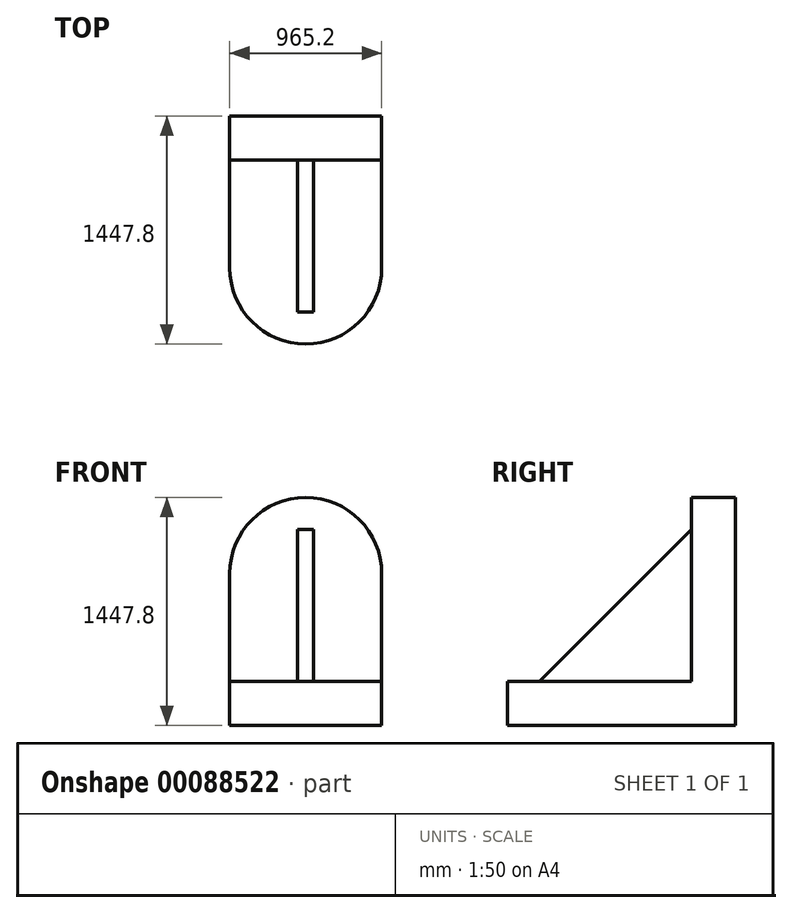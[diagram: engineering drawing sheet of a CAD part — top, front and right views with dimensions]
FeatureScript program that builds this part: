
annotation { "Feature Type Name" : "Feature", "Feature Type Description" : "" }
export const myFeature = defineFeature(function(context is Context, id is Id, definition is map)
    precondition{}
    {
        {
            var Q0;
            Q0=qCreatedBy(makeId("Top.planeOp"),FACE);
            var sketch = newSketch(context, id + "F0", { "sketchPlane" : qUnion([Q0])});
            skLineSegment(sketch, "E0.bottom", {"start": v(-482.6, 482.6) * mm, "end": v(482.6, 482.6) * mm});
            skLineSegment(sketch, "E0.top", {"start": v(-482.6, -482.6) * mm, "end": v(482.6, -482.6) * mm});
            skLineSegment(sketch, "E0.left", {"start": v(-482.6, 482.6) * mm, "end": v(-482.6, -482.6) * mm});
            skLineSegment(sketch, "E0.right", {"start": v(482.6, 482.6) * mm, "end": v(482.6, -482.6) * mm});
            skSolve(sketch);
        }
        {
            var Q0;
            Q0=makeQuery(id+"F0.imprint","IMPRINT",FACE,{"disambiguationData":[TD([[makeQuery(id+"F0.imprint","IMPRINT",EDGE,{"derivedFrom":sQuery(id+"F0.wireOp",EDGE,"E0.bottom")}),-1.0]])]});
            extrude(context, id + "F1", {"entities" : qUnion([Q0]), "endBound" : BoundingType.SYMMETRIC, "depth" : 965.2 * mm});
        }
        {
            var Q0;
            Q0=makeQuery(id+"F1.opExtrude","SWEPT_FACE",FACE,{"disambiguationData":[OSD([sQuery(id+"F0.wireOp",EDGE,"E0.left")])]});
            var sketch = newSketch(context, id + "F2", { "sketchPlane" : qUnion([Q0])});
            skLineSegment(sketch, "E1.bottom", {"start": v(-203.2, 482.6) * mm, "end": v(482.6, 482.6) * mm});
            skLineSegment(sketch, "E1.top", {"start": v(-203.2, -203.2) * mm, "end": v(482.6, -203.2) * mm});
            skLineSegment(sketch, "E1.left", {"start": v(-203.2, 482.6) * mm, "end": v(-203.2, -203.2) * mm});
            skLineSegment(sketch, "E1.right", {"start": v(482.6, 482.6) * mm, "end": v(482.6, -203.2) * mm});
            skSolve(sketch);
        }
        {
            var Q0;
            Q0=makeQuery(id+"F2.imprint","IMPRINT",FACE,{"disambiguationData":[TD([[makeQuery(id+"F2.imprint","IMPRINT",EDGE,{"derivedFrom":sQuery(id+"F2.wireOp",EDGE,"E1.bottom")}),-1.0]])]});
            extrude(context, id + "F3", {"entities" : qUnion([Q0]), "operationType" : NewBodyOperationType.REMOVE, "endBound" : BoundingType.THROUGH_ALL, "oppositeDirection" : true, "depth" : 25.4 * mm});
        }
        {
            var Q0;
            Q0=makeQuery(id+"F3.boolean.opBoolean","COPY",FACE,{"derivedFrom":makeQuery(id+"F3.opExtrude","SWEPT_FACE",FACE,{"disambiguationData":[OSD([sQuery(id+"F2.wireOp",EDGE,"E1.left")])]})});
            var sketch = newSketch(context, id + "F4", { "sketchPlane" : qUnion([Q0])});
            skArc(sketch, "E2", {"start": v(482.6, 482.6) * mm, "mid": v(0, 965.2) * mm, "end": v(-482.6, 482.6) * mm});
            skSolve(sketch);
        }
        {
            var Q0;
            Q0=makeQuery(id+"F4.imprint","IMPRINT",FACE,{"disambiguationData":[TD([[makeQuery(id+"F4.imprint","IMPRINT",EDGE,{"derivedFrom":sQuery(id+"F4.wireOp",EDGE,"E2")}),1.0]])]});
            var Q1;
            Q1=makeQuery(id+"F1.opExtrude","SWEPT_FACE",FACE,{"disambiguationData":[OSD([sQuery(id+"F0.wireOp",EDGE,"E0.bottom")])]});
            extrude(context, id + "F5", {"entities" : qUnion([Q0]), "operationType" : NewBodyOperationType.ADD, "endBound" : BoundingType.UP_TO_SURFACE, "oppositeDirection" : true, "endBoundEntityFace" : qUnion([Q1]), "depth" : 25.4 * mm});
        }
        {
            var Q0;
            Q0=makeQuery(id+"F3.boolean.opBoolean","COPY",FACE,{"derivedFrom":makeQuery(id+"F3.opExtrude","SWEPT_FACE",FACE,{"disambiguationData":[OSD([sQuery(id+"F2.wireOp",EDGE,"E1.top")])]})});
            var sketch = newSketch(context, id + "F6", { "sketchPlane" : qUnion([Q0])});
            skArc(sketch, "E3", {"start": v(-482.6, -482.6) * mm, "mid": v(0, -965.2) * mm, "end": v(482.6, -482.6) * mm});
            skSolve(sketch);
        }
        {
            var Q0;
            Q0=makeQuery(id+"F6.imprint","IMPRINT",FACE,{"disambiguationData":[TD([[makeQuery(id+"F6.imprint","IMPRINT",EDGE,{"derivedFrom":sQuery(id+"F6.wireOp",EDGE,"E3")}),1.0]])]});
            var Q1;
            Q1=makeQuery(id+"F1.opExtrude","CAP_FACE",FACE,{"disambiguationData":[OSD([sQuery(id+"F0.wireOp",EDGE,"E0.bottom"),sQuery(id+"F0.wireOp",EDGE,"E0.top"),sQuery(id+"F0.wireOp",EDGE,"E0.left"),sQuery(id+"F0.wireOp",EDGE,"E0.right")])],"isStart":true});
            extrude(context, id + "F7", {"entities" : qUnion([Q0]), "operationType" : NewBodyOperationType.ADD, "endBound" : BoundingType.UP_TO_SURFACE, "oppositeDirection" : true, "endBoundEntityFace" : qUnion([Q1]), "depth" : 25.4 * mm});
        }
        {
            var Q0;
            Q0=qCreatedBy(makeId("Right.planeOp"),FACE);
            var sketch = newSketch(context, id + "F8", { "sketchPlane" : qUnion([Q0])});
            skLineSegment(sketch, "E4", {"start": v(203.2, -203.2) * mm, "end": v(-762, -203.2) * mm});
            skLineSegment(sketch, "E5", {"start": v(-762, -203.2) * mm, "end": v(203.2, 762) * mm});
            skLineSegment(sketch, "E6", {"start": v(203.2, 762) * mm, "end": v(203.2, -203.2) * mm});
            skSolve(sketch);
        }
        {
            var Q0;
            Q0=makeQuery(id+"F8.imprint","IMPRINT",FACE,{"disambiguationData":[TD([[makeQuery(id+"F8.imprint","IMPRINT",EDGE,{"derivedFrom":sQuery(id+"F8.wireOp",EDGE,"E4")}),-1.0]])]});
            extrude(context, id + "F9", {"entities" : qUnion([Q0]), "operationType" : NewBodyOperationType.ADD, "endBound" : BoundingType.SYMMETRIC, "depth" : 101.6 * mm});
        }
    });
